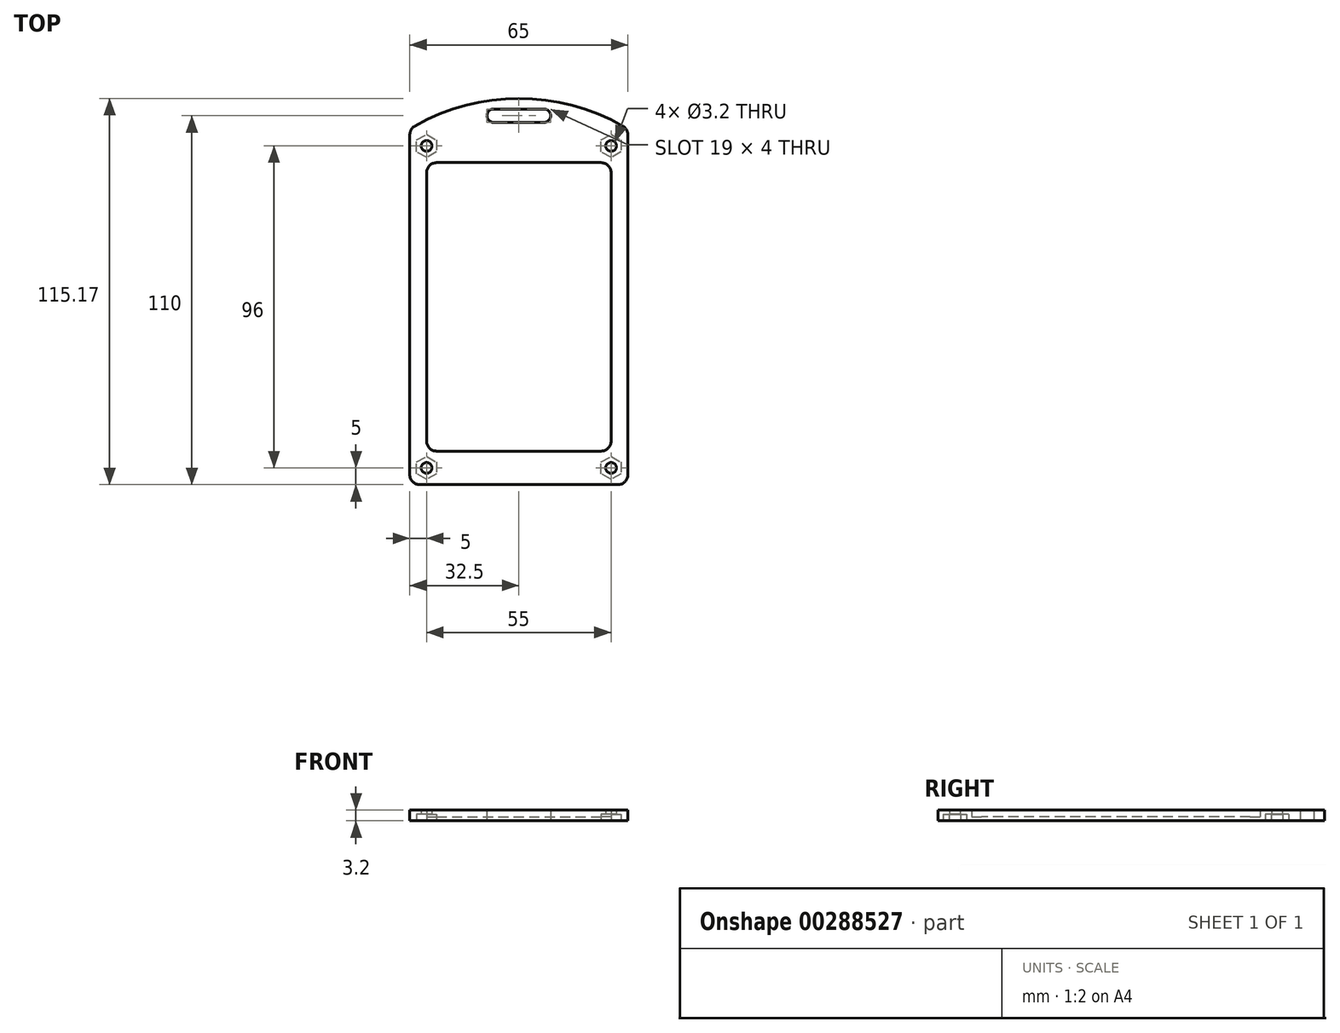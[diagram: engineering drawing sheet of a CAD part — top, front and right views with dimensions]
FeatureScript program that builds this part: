
annotation { "Feature Type Name" : "Feature", "Feature Type Description" : "" }
export const myFeature = defineFeature(function(context is Context, id is Id, definition is map)
    precondition{}
    {
        {
            var Q0;
            Q0=qCreatedBy(makeId("Top.planeOp"),FACE);
            var sketch = newSketch(context, id + "F0", { "sketchPlane" : qUnion([Q0])});
            skLineSegment(sketch, "E0.bottom", {"start": v(-24.5, 43) * mm, "end": v(24.5, 43) * mm});
            skLineSegment(sketch, "E0.top", {"start": v(-24.5, -43) * mm, "end": v(24.5, -43) * mm});
            skLineSegment(sketch, "E0.left", {"start": v(-27.5, 40) * mm, "end": v(-27.5, -40) * mm});
            skLineSegment(sketch, "E0.right", {"start": v(27.5, 40) * mm, "end": v(27.5, -40) * mm});
            skPoint(sketch, "E0.middle", {"position": v(0, 0) * mm});
            skLineSegment(sketch, "E1.1", {"start": v(-32.5, 48) * mm, "end": v(-32.5, -48) * mm});
            skLineSegment(sketch, "E1.3", {"start": v(32.5, 48) * mm, "end": v(32.5, -48) * mm});
            skLineSegment(sketch, "E2.top", {"start": v(-29.5, -53) * mm, "end": v(29.5, -53) * mm});
            skLineSegment(sketch, "E2.left", {"start": v(-32.5, -48) * mm, "end": v(-32.5, -50) * mm});
            skLineSegment(sketch, "E2.right", {"start": v(32.5, -48) * mm, "end": v(32.5, -50) * mm});
            skLineSegment(sketch, "E3.left", {"start": v(-32.5, 48) * mm, "end": v(-32.5, 51.3) * mm});
            skLineSegment(sketch, "E3.right", {"start": v(32.5, 48) * mm, "end": v(32.5, 51.3) * mm});
            skPoint(sketch, "E4.visualSharp", {"position": v(-27.5, 43) * mm});
            skArc(sketch, "E4.filletArc", {"start": v(-24.5, 43) * mm, "mid": v(-26.62, 42.12) * mm, "end": v(-27.5, 40) * mm});
            skPoint(sketch, "E5.visualSharp", {"position": v(27.5, 43) * mm});
            skArc(sketch, "E5.filletArc", {"start": v(27.5, 40) * mm, "mid": v(26.62, 42.12) * mm, "end": v(24.5, 43) * mm});
            skPoint(sketch, "E6.visualSharp", {"position": v(27.5, -43) * mm});
            skArc(sketch, "E6.filletArc", {"start": v(24.5, -43) * mm, "mid": v(26.62, -42.12) * mm, "end": v(27.5, -40) * mm});
            skPoint(sketch, "E7.visualSharp", {"position": v(-27.5, -43) * mm});
            skArc(sketch, "E7.filletArc", {"start": v(-27.5, -40) * mm, "mid": v(-26.62, -42.12) * mm, "end": v(-24.5, -43) * mm});
            skArc(sketch, "E8", {"start": v(-31, 53.9) * mm, "mid": v(0, 62.17) * mm, "end": v(31, 53.9) * mm});
            skPoint(sketch, "E9.visualSharp", {"position": v(-32.5, -53) * mm});
            skArc(sketch, "E9.filletArc", {"start": v(-32.5, -50) * mm, "mid": v(-31.62, -52.12) * mm, "end": v(-29.5, -53) * mm});
            skPoint(sketch, "E10.visualSharp", {"position": v(32.5, -53) * mm});
            skArc(sketch, "E10.filletArc", {"start": v(29.5, -53) * mm, "mid": v(31.62, -52.12) * mm, "end": v(32.5, -50) * mm});
            skCircle(sketch, "E11", {"center": v(-27.5, 48) * mm, "radius": 1.6 * mm});
            skCircle(sketch, "E12", {"center": v(27.5, 48) * mm, "radius": 1.6 * mm});
            skCircle(sketch, "E13", {"center": v(27.5, -48) * mm, "radius": 1.6 * mm});
            skCircle(sketch, "E14", {"center": v(-27.5, -48) * mm, "radius": 1.6 * mm});
            skLineSegment(sketch, "E15.bottom", {"start": v(-7.5, 59) * mm, "end": v(7.5, 59) * mm});
            skLineSegment(sketch, "E15.top", {"start": v(-7.5, 55) * mm, "end": v(7.5, 55) * mm});
            skArc(sketch, "E16", {"start": v(-7.5, 55) * mm, "mid": v(-9.5, 57) * mm, "end": v(-7.5, 59) * mm});
            skArc(sketch, "E17", {"start": v(7.5, 59) * mm, "mid": v(9.5, 57) * mm, "end": v(7.5, 55) * mm});
            skCircle(sketch, "E18.cCircle", {"center": v(-27.5, 48) * mm, "radius": 3 * mm, "construction": true});
            skLineSegment(sketch, "E18.0", {"start": v(-24.5, 49.73) * mm, "end": v(-24.5, 46.27) * mm});
            skLineSegment(sketch, "E18.1", {"start": v(-24.5, 46.27) * mm, "end": v(-27.5, 44.54) * mm});
            skLineSegment(sketch, "E18.2", {"start": v(-27.5, 44.54) * mm, "end": v(-30.5, 46.27) * mm});
            skLineSegment(sketch, "E18.3", {"start": v(-30.5, 46.27) * mm, "end": v(-30.5, 49.73) * mm});
            skLineSegment(sketch, "E18.4", {"start": v(-30.5, 49.73) * mm, "end": v(-27.5, 51.46) * mm});
            skLineSegment(sketch, "E18.5", {"start": v(-27.5, 51.46) * mm, "end": v(-24.5, 49.73) * mm});
            skPoint(sketch, "E18.0.midPoint", {"position": v(-24.5, 48) * mm});
            skCircle(sketch, "E19.cCircle", {"center": v(27.5, 48) * mm, "radius": 3 * mm, "construction": true});
            skLineSegment(sketch, "E19.0", {"start": v(24.5, 46.27) * mm, "end": v(24.5, 49.73) * mm});
            skLineSegment(sketch, "E19.1", {"start": v(24.5, 49.73) * mm, "end": v(27.5, 51.46) * mm});
            skLineSegment(sketch, "E19.2", {"start": v(27.5, 51.46) * mm, "end": v(30.5, 49.73) * mm});
            skLineSegment(sketch, "E19.3", {"start": v(30.5, 49.73) * mm, "end": v(30.5, 46.27) * mm});
            skLineSegment(sketch, "E19.4", {"start": v(30.5, 46.27) * mm, "end": v(27.5, 44.54) * mm});
            skLineSegment(sketch, "E19.5", {"start": v(27.5, 44.54) * mm, "end": v(24.5, 46.27) * mm});
            skPoint(sketch, "E19.0.midPoint", {"position": v(24.5, 48) * mm});
            skCircle(sketch, "E20.cCircle", {"center": v(27.5, -48) * mm, "radius": 3 * mm, "construction": true});
            skLineSegment(sketch, "E20.0", {"start": v(24.5, -49.73) * mm, "end": v(24.5, -46.27) * mm});
            skLineSegment(sketch, "E20.1", {"start": v(24.5, -46.27) * mm, "end": v(27.5, -44.54) * mm});
            skLineSegment(sketch, "E20.2", {"start": v(27.5, -44.54) * mm, "end": v(30.5, -46.27) * mm});
            skLineSegment(sketch, "E20.3", {"start": v(30.5, -46.27) * mm, "end": v(30.5, -49.73) * mm});
            skLineSegment(sketch, "E20.4", {"start": v(30.5, -49.73) * mm, "end": v(27.5, -51.46) * mm});
            skLineSegment(sketch, "E20.5", {"start": v(27.5, -51.46) * mm, "end": v(24.5, -49.73) * mm});
            skPoint(sketch, "E20.0.midPoint", {"position": v(24.5, -48) * mm});
            skCircle(sketch, "E21.cCircle", {"center": v(-27.5, -48) * mm, "radius": 3 * mm, "construction": true});
            skLineSegment(sketch, "E21.0", {"start": v(-24.5, -46.27) * mm, "end": v(-24.5, -49.73) * mm});
            skLineSegment(sketch, "E21.1", {"start": v(-24.5, -49.73) * mm, "end": v(-27.5, -51.46) * mm});
            skLineSegment(sketch, "E21.2", {"start": v(-27.5, -51.46) * mm, "end": v(-30.5, -49.73) * mm});
            skLineSegment(sketch, "E21.3", {"start": v(-30.5, -49.73) * mm, "end": v(-30.5, -46.27) * mm});
            skLineSegment(sketch, "E21.4", {"start": v(-30.5, -46.27) * mm, "end": v(-27.5, -44.54) * mm});
            skLineSegment(sketch, "E21.5", {"start": v(-27.5, -44.54) * mm, "end": v(-24.5, -46.27) * mm});
            skPoint(sketch, "E21.0.midPoint", {"position": v(-24.5, -48) * mm});
            skPoint(sketch, "E22.visualSharp", {"position": v(-32.5, 53) * mm});
            skArc(sketch, "E22.filletArc", {"start": v(-31, 53.9) * mm, "mid": v(-32.1, 52.8) * mm, "end": v(-32.5, 51.3) * mm});
            skPoint(sketch, "E23.visualSharp", {"position": v(32.5, 53) * mm});
            skArc(sketch, "E23.filletArc", {"start": v(32.5, 51.3) * mm, "mid": v(32.1, 52.8) * mm, "end": v(31, 53.9) * mm});
            skSolve(sketch);
        }
        {
            var Q0;
            Q0 = qSketchRegion(id + "F0", true);
            extrude(context, id + "F1", {"entities" : qUnion([Q0]), "depth" : 3.2 * mm});
        }
        {
            var Q0;
            Q0=makeQuery(id+"F0.imprint","IMPRINT",FACE,{"disambiguationData":[TD([[makeQuery(id+"F0.imprint","IMPRINT",EDGE,{"derivedFrom":sQuery(id+"F0.wireOp",EDGE,"E0.bottom")}),-1.0]])]});
            extrude(context, id + "F2", {"entities" : qUnion([Q0]), "operationType" : NewBodyOperationType.ADD, "depth" : 1.2 * mm});
        }
        {
            var Q0;
            {var subQ9=sQuery(id+"F0.wireOp",EDGE,"E21.4");Q0=makeQuery(id+"F0.imprint","IMPRINT",FACE,{"disambiguationData":[TD([[makeQuery(id+"F0.imprint","IMPRINT",EDGE,{"derivedFrom":subQ9}),-1.0]])]});}
            var Q1;
            {var subQ0=sQuery(id+"F0.wireOp",EDGE,"E21.1");Q1=makeQuery(id+"F0.imprint","IMPRINT",FACE,{"disambiguationData":[TD([[makeQuery(id+"F0.imprint","IMPRINT",EDGE,{"derivedFrom":subQ0}),-1.0]])]});}
            var Q2;
            {var subQ0=sQuery(id+"F0.wireOp",EDGE,"E20.1");Q2=makeQuery(id+"F0.imprint","IMPRINT",FACE,{"disambiguationData":[TD([[makeQuery(id+"F0.imprint","IMPRINT",EDGE,{"derivedFrom":subQ0}),-1.0]])]});}
            var Q3;
            {var subQ9=sQuery(id+"F0.wireOp",EDGE,"E20.4");Q3=makeQuery(id+"F0.imprint","IMPRINT",FACE,{"disambiguationData":[TD([[makeQuery(id+"F0.imprint","IMPRINT",EDGE,{"derivedFrom":subQ9}),-1.0]])]});}
            var Q4;
            {var subQ9=sQuery(id+"F0.wireOp",EDGE,"E19.4");Q4=makeQuery(id+"F0.imprint","IMPRINT",FACE,{"disambiguationData":[TD([[makeQuery(id+"F0.imprint","IMPRINT",EDGE,{"derivedFrom":subQ9}),-1.0]])]});}
            var Q5;
            {var subQ4=sQuery(id+"F0.wireOp",EDGE,"E19.1");Q5=makeQuery(id+"F0.imprint","IMPRINT",FACE,{"disambiguationData":[TD([[makeQuery(id+"F0.imprint","IMPRINT",EDGE,{"derivedFrom":subQ4}),-1.0]])]});}
            var Q6;
            {var subQ0=sQuery(id+"F0.wireOp",EDGE,"E18.1");Q6=makeQuery(id+"F0.imprint","IMPRINT",FACE,{"disambiguationData":[TD([[makeQuery(id+"F0.imprint","IMPRINT",EDGE,{"derivedFrom":subQ0}),-1.0]])]});}
            var Q7;
            {var subQ9=sQuery(id+"F0.wireOp",EDGE,"E18.4");Q7=makeQuery(id+"F0.imprint","IMPRINT",FACE,{"disambiguationData":[TD([[makeQuery(id+"F0.imprint","IMPRINT",EDGE,{"derivedFrom":subQ9}),-1.0]])]});}
            extrude(context, id + "F3", {"entities" : qUnion([Q0, Q1, Q2, Q3, Q4, Q5, Q6, Q7]), "operationType" : NewBodyOperationType.ADD, "depth" : 3.2 * mm, "hasSecondDirection" : true, "secondDirectionOppositeDirection" : false, "secondDirectionDepth" : 2 * mm});
        }
    });
